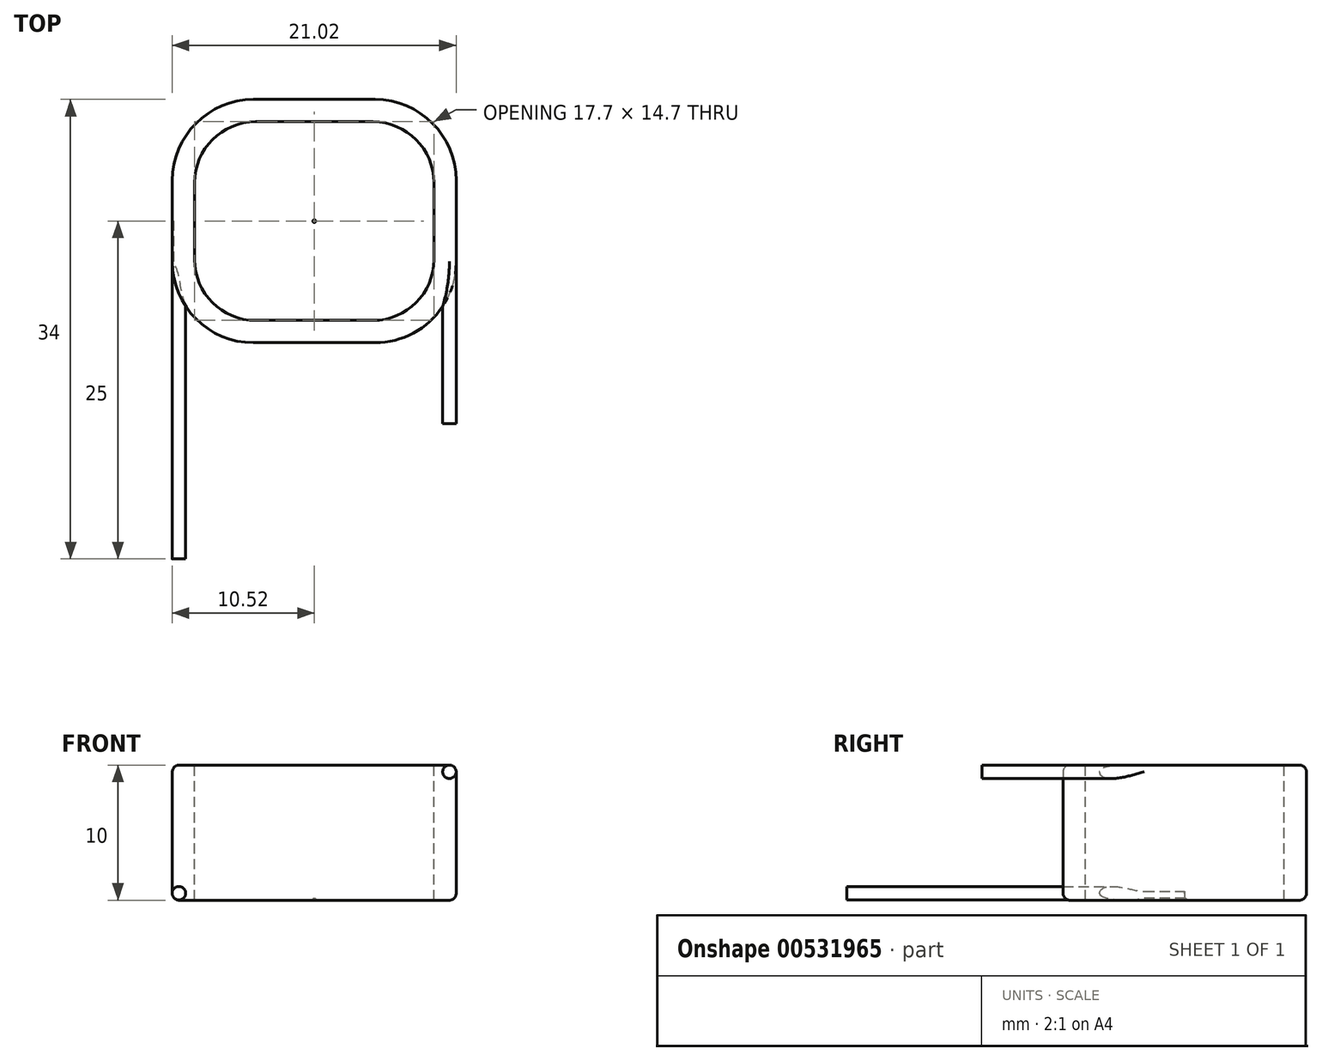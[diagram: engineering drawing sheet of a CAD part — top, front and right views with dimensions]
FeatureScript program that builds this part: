
annotation { "Feature Type Name" : "Feature", "Feature Type Description" : "" }
export const myFeature = defineFeature(function(context is Context, id is Id, definition is map)
    precondition{}
    {
        {
            var Q0;
            Q0=qCreatedBy(makeId("Top.planeOp"),FACE);
            var sketch = newSketch(context, id + "F0", { "sketchPlane" : qUnion([Q0])});
            skLineSegment(sketch, "E0.bottom", {"start": v(4.5, -9) * mm, "end": v(-4.5, -9) * mm});
            skLineSegment(sketch, "E0.top", {"start": v(4.5, 9) * mm, "end": v(-4.5, 9) * mm});
            skLineSegment(sketch, "E0.left", {"start": v(10.5, -3) * mm, "end": v(10.5, 3) * mm});
            skLineSegment(sketch, "E0.right", {"start": v(-10.5, -3) * mm, "end": v(-10.5, 3) * mm});
            skPoint(sketch, "E0.middle", {"position": v(0, 0) * mm});
            skPoint(sketch, "E1.visualSharp", {"position": v(-10.5, 9) * mm});
            skArc(sketch, "E1.filletArc", {"start": v(-4.5, 9) * mm, "mid": v(-8.74, 7.24) * mm, "end": v(-10.5, 3) * mm});
            skPoint(sketch, "E2.visualSharp", {"position": v(-10.5, -9) * mm});
            skArc(sketch, "E2.filletArc", {"start": v(-10.5, -3) * mm, "mid": v(-8.74, -7.24) * mm, "end": v(-4.5, -9) * mm});
            skPoint(sketch, "E3.visualSharp", {"position": v(10.5, -9) * mm});
            skArc(sketch, "E3.filletArc", {"start": v(4.5, -9) * mm, "mid": v(8.74, -7.24) * mm, "end": v(10.5, -3) * mm});
            skPoint(sketch, "E4.visualSharp", {"position": v(10.5, 9) * mm});
            skArc(sketch, "E4.filletArc", {"start": v(10.5, 3) * mm, "mid": v(8.74, 7.24) * mm, "end": v(4.5, 9) * mm});
            skSolve(sketch);
        }
        {
            var Q0;
            Q0=qSketchRegion(id+"F0",true);
            extrude(context, id + "F1", {"entities" : qUnion([Q0]), "depth" : 10 * mm, "offsetDistance" : 25 * mm});
        }
        {
            var Q0;
            Q0=makeQuery(id+"F1.opExtrude","CAP_FACE",FACE,{"disambiguationData":[OSD([sQuery(id+"F0.wireOp",EDGE,"E0.bottom"),sQuery(id+"F0.wireOp",EDGE,"E0.top"),sQuery(id+"F0.wireOp",EDGE,"E0.left"),sQuery(id+"F0.wireOp",EDGE,"E0.right"),sQuery(id+"F0.wireOp",EDGE,"E1.filletArc"),sQuery(id+"F0.wireOp",EDGE,"E2.filletArc"),sQuery(id+"F0.wireOp",EDGE,"E3.filletArc"),sQuery(id+"F0.wireOp",EDGE,"E4.filletArc")])],"isStart":false});
            var sketch = newSketch(context, id + "F2", { "sketchPlane" : qUnion([Q0])});
            skLineSegment(sketch, "E5.bottom", {"start": v(4.35, -7.35) * mm, "end": v(-4.35, -7.35) * mm});
            skLineSegment(sketch, "E5.top", {"start": v(4.35, 7.35) * mm, "end": v(-4.35, 7.35) * mm});
            skLineSegment(sketch, "E5.left", {"start": v(8.85, -2.85) * mm, "end": v(8.85, 2.85) * mm});
            skLineSegment(sketch, "E5.right", {"start": v(-8.85, -2.85) * mm, "end": v(-8.85, 2.85) * mm});
            skPoint(sketch, "E5.middle", {"position": v(0, 0) * mm});
            skPoint(sketch, "E6.visualSharp", {"position": v(-8.85, 7.35) * mm});
            skArc(sketch, "E6.filletArc", {"start": v(-4.35, 7.35) * mm, "mid": v(-7.53, 6.03) * mm, "end": v(-8.85, 2.85) * mm});
            skPoint(sketch, "E7.visualSharp", {"position": v(-8.85, -7.35) * mm});
            skArc(sketch, "E7.filletArc", {"start": v(-8.85, -2.85) * mm, "mid": v(-7.53, -6.03) * mm, "end": v(-4.35, -7.35) * mm});
            skPoint(sketch, "E8.visualSharp", {"position": v(8.85, -7.35) * mm});
            skArc(sketch, "E8.filletArc", {"start": v(4.35, -7.35) * mm, "mid": v(7.53, -6.03) * mm, "end": v(8.85, -2.85) * mm});
            skPoint(sketch, "E9.visualSharp", {"position": v(8.85, 7.35) * mm});
            skArc(sketch, "E9.filletArc", {"start": v(8.85, 2.85) * mm, "mid": v(7.53, 6.03) * mm, "end": v(4.35, 7.35) * mm});
            skSolve(sketch);
        }
        {
            var Q0;
            Q0=qSketchRegion(id+"F2",true);
            extrude(context, id + "F3", {"entities" : qUnion([Q0]), "operationType" : NewBodyOperationType.REMOVE, "oppositeDirection" : true, "depth" : 10 * mm, "offsetDistance" : 25 * mm});
        }
        {
            var Q0;
            Q0=makeQuery(id+"F1.opExtrude","CAP_EDGE",EDGE,{"disambiguationData":[OSD([sQuery(id+"F0.wireOp",EDGE,"E1.filletArc")])],"isStart":false});
            var Q1;
            Q1=makeQuery(id+"F3.boolean.opBoolean","COPY",EDGE,{"derivedFrom":makeQuery(id+"F3.opExtrude","CAP_EDGE",EDGE,{"disambiguationData":[OSD([sQuery(id+"F2.wireOp",EDGE,"E5.left")])],"isStart":true})});
            var Q2;
            Q2=makeQuery(id+"F1.opExtrude","CAP_EDGE",EDGE,{"disambiguationData":[OSD([sQuery(id+"F0.wireOp",EDGE,"E1.filletArc")])],"isStart":true});
            var Q3;
            Q3=makeQuery(id+"F3.boolean.opBoolean","COPY",EDGE,{"derivedFrom":makeQuery(id+"F3.opExtrude","CAP_EDGE",EDGE,{"disambiguationData":[OSD([sQuery(id+"F2.wireOp",EDGE,"E9.filletArc")])],"isStart":false})});
            fillet(context, id + "F4", {"entities" : qUnion([Q0, Q1, Q2, Q3]), "radius" : 0.5 * mm, "tangentPropagation" : true, "allowEdgeOverflow" : false});
        }
        {
            var Q0;
            Q0=qCreatedBy(makeId("Top.planeOp"),FACE);
            var sketch = newSketch(context, id + "F5", { "sketchPlane" : qUnion([Q0])});
            skCircle(sketch, "E10", {"center": v(0, 0) * mm, "radius": 0.1 * mm});
            skSolve(sketch);
        }
        {
            var Q0;
            Q0=qSketchRegion(id+"F5",true);
            extrude(context, id + "F6", {"entities" : qUnion([Q0]), "depth" : 0.1 * mm});
        }
        {
            var Q0;
            Q0=qCreatedBy(makeId("Front.planeOp"),FACE);
            var sketch = newSketch(context, id + "F7", { "sketchPlane" : qUnion([Q0])});
            skCircle(sketch, "E11", {"center": v(-10.02, 0.52) * mm, "radius": 0.5 * mm});
            skSolve(sketch);
        }
        {
            var Q0;
            Q0=qSketchRegion(id+"F7",true);
            extrude(context, id + "F8", {"entities" : qUnion([Q0]), "operationType" : NewBodyOperationType.ADD, "depth" : 25 * mm});
        }
        {
            var Q0;
            Q0=qCreatedBy(makeId("Front.planeOp"),FACE);
            var sketch = newSketch(context, id + "F9", { "sketchPlane" : qUnion([Q0])});
            skCircle(sketch, "E12", {"center": v(10, 9.5) * mm, "radius": 0.5 * mm});
            skSolve(sketch);
        }
        {
            var Q0;
            Q0=qSketchRegion(id+"F9",true);
            extrude(context, id + "F10", {"entities" : qUnion([Q0]), "operationType" : NewBodyOperationType.ADD, "depth" : 15 * mm});
        }
    });
